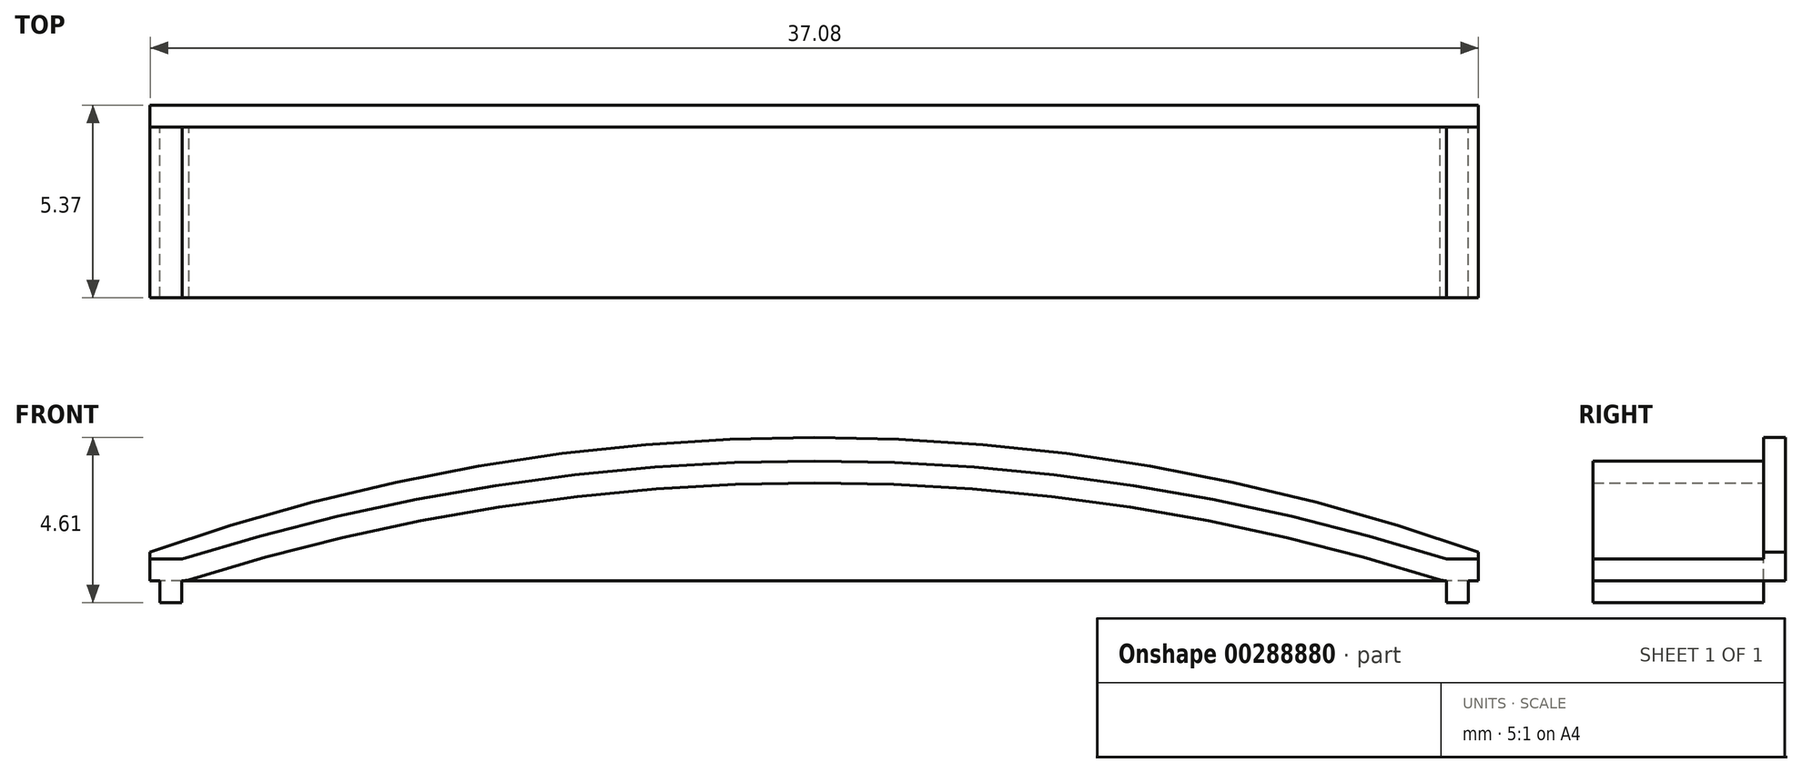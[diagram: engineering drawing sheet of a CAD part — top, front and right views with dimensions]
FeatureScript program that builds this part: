
annotation { "Feature Type Name" : "Feature", "Feature Type Description" : "" }
export const myFeature = defineFeature(function(context is Context, id is Id, definition is map)
    precondition{}
    {
        {
            var Q0;
            Q0=qCreatedBy(makeId("Front.planeOp"),FACE);
            var sketch = newSketch(context, id + "F0", { "sketchPlane" : qUnion([Q0])});
            skLineSegment(sketch, "E0", {"start": v(0, 0) * mm, "end": v(-37.08, 0) * mm});
            skPoint(sketch, "E1", {"position": v(-18.54, 0) * mm});
            skLineSegment(sketch, "E2", {"start": v(-37.08, 0) * mm, "end": v(-37.08, 0.8) * mm});
            skLineSegment(sketch, "E3", {"start": v(0, 0) * mm, "end": v(0, 0.8) * mm});
            skPoint(sketch, "E4", {"position": v(-18.54, 3.97) * mm});
            skArc(sketch, "E5", {"start": v(0, 0.8) * mm, "mid": v(-18.54, 4) * mm, "end": v(-37.08, 0.8) * mm});
            skSolve(sketch);
        }
        {
            var Q0;
            Q0=makeQuery(id+"F0.imprint","IMPRINT",FACE,{"disambiguationData":[TD([[makeQuery(id+"F0.imprint","IMPRINT",EDGE,{"derivedFrom":sQuery(id+"F0.wireOp",EDGE,"E0")}),-1.0]])]});
            extrude(context, id + "F1", {"entities" : qUnion([Q0]), "oppositeDirection" : true, "depth" : 0.6 * mm});
        }
        {
            var Q0;
            Q0=makeQuery(id+"F1.opExtrude","CAP_FACE",FACE,{"disambiguationData":[OSD([sQuery(id+"F0.wireOp",EDGE,"E0"),sQuery(id+"F0.wireOp",EDGE,"E2"),sQuery(id+"F0.wireOp",EDGE,"E3"),sQuery(id+"F0.wireOp",EDGE,"E5")])],"isStart":true});
            var sketch = newSketch(context, id + "F2", { "sketchPlane" : qUnion([Q0])});
            skLineSegment(sketch, "E6", {"start": v(-37.08, 0) * mm, "end": v(-36.8, 0) * mm});
            skLineSegment(sketch, "E7", {"start": v(-36.8, 0) * mm, "end": v(-36.8, -0.6) * mm});
            skLineSegment(sketch, "E8", {"start": v(-36.8, -0.6) * mm, "end": v(-36.2, -0.6) * mm});
            skLineSegment(sketch, "E9", {"start": v(-36.2, -0.6) * mm, "end": v(-36.2, 0) * mm});
            skLineSegment(sketch, "E10", {"start": v(-37.08, 0) * mm, "end": v(-37.08, 0.6) * mm});
            skLineSegment(sketch, "E11", {"start": v(-37.08, 0.6) * mm, "end": v(-36.18, 0.6) * mm});
            skLineSegment(sketch, "E12", {"start": v(-36.18, 0.6) * mm, "end": v(-36.2, 0) * mm});
            skLineSegment(sketch, "E13", {"start": v(0, 0) * mm, "end": v(-0.28, 0) * mm});
            skLineSegment(sketch, "E14", {"start": v(-0.28, 0) * mm, "end": v(-0.28, -0.6) * mm});
            skLineSegment(sketch, "E15", {"start": v(-0.28, -0.6) * mm, "end": v(-0.89, -0.6) * mm});
            skLineSegment(sketch, "E16", {"start": v(0, 0) * mm, "end": v(0, 0.6) * mm});
            skLineSegment(sketch, "E17", {"start": v(-0.89, -0.6) * mm, "end": v(-0.89, 0.6) * mm});
            skLineSegment(sketch, "E18", {"start": v(-0.89, 0.6) * mm, "end": v(0, 0.6) * mm});
            skSolve(sketch);
        }
        {
            var Q0;
            {var subQ1=sQuery(id+"F2.wireOp",EDGE,"E6");Q0=makeQuery(id+"F2.imprint","IMPRINT",FACE,{"disambiguationData":[TD([[makeQuery(id+"F2.imprint","IMPRINT",EDGE,{"derivedFrom":subQ1}),-1.0]])]});}
            var Q1;
            {var subQ0=sQuery(id+"F2.wireOp",EDGE,"E7");Q1=makeQuery(id+"F2.imprint","IMPRINT",FACE,{"disambiguationData":[TD([[makeQuery(id+"F2.imprint","IMPRINT",EDGE,{"derivedFrom":subQ0}),1.0]])]});}
            var Q2;
            {var subQ0=sQuery(id+"F2.wireOp",EDGE,"E14");Q2=makeQuery(id+"F2.imprint","IMPRINT",FACE,{"disambiguationData":[TD([[makeQuery(id+"F2.imprint","IMPRINT",EDGE,{"derivedFrom":subQ0}),-1.0]])]});}
            var Q3;
            {var subQ4=sQuery(id+"F2.wireOp",EDGE,"E13");Q3=makeQuery(id+"F2.imprint","IMPRINT",FACE,{"disambiguationData":[TD([[makeQuery(id+"F2.imprint","IMPRINT",EDGE,{"derivedFrom":subQ4}),-1.0]])]});}
            extrude(context, id + "F3", {"entities" : qUnion([Q0, Q1, Q2, Q3]), "operationType" : NewBodyOperationType.ADD, "depth" : 4.76 * mm});
        }
        {
            var Q0;
            Q0=makeQuery(id+"F1.opExtrude","CAP_FACE",FACE,{"disambiguationData":[OSD([sQuery(id+"F0.wireOp",EDGE,"E0"),sQuery(id+"F0.wireOp",EDGE,"E2"),sQuery(id+"F0.wireOp",EDGE,"E3"),sQuery(id+"F0.wireOp",EDGE,"E5")])],"isStart":true});
            var sketch = newSketch(context, id + "F4", { "sketchPlane" : qUnion([Q0])});
            skArc(sketch, "E19", {"start": v(-0.89, 0.6) * mm, "mid": v(-18.54, 3.34) * mm, "end": v(-36.18, 0.6) * mm});
            skArc(sketch, "E20.0", {"start": v(-1.07, 0.03) * mm, "mid": v(-18.54, 2.73) * mm, "end": v(-36, 0.03) * mm});
            skLineSegment(sketch, "E21", {"start": v(-36, 0.03) * mm, "end": v(-36.2, 0) * mm});
            skLineSegment(sketch, "E22", {"start": v(-36.2, 0) * mm, "end": v(-36.18, 0.6) * mm});
            skLineSegment(sketch, "E23", {"start": v(-1.07, 0.03) * mm, "end": v(-0.89, 0) * mm});
            skLineSegment(sketch, "E24", {"start": v(-0.89, 0) * mm, "end": v(-0.89, 0.6) * mm});
            skSolve(sketch);
        }
        {
            var Q0;
            Q0=makeQuery(id+"F4.imprint","IMPRINT",FACE,{"disambiguationData":[TD([[makeQuery(id+"F4.imprint","IMPRINT",EDGE,{"derivedFrom":sQuery(id+"F4.wireOp",EDGE,"E19")}),1.0]])]});
            extrude(context, id + "F5", {"entities" : qUnion([Q0]), "operationType" : NewBodyOperationType.ADD, "depth" : 4.76 * mm});
        }
    });
